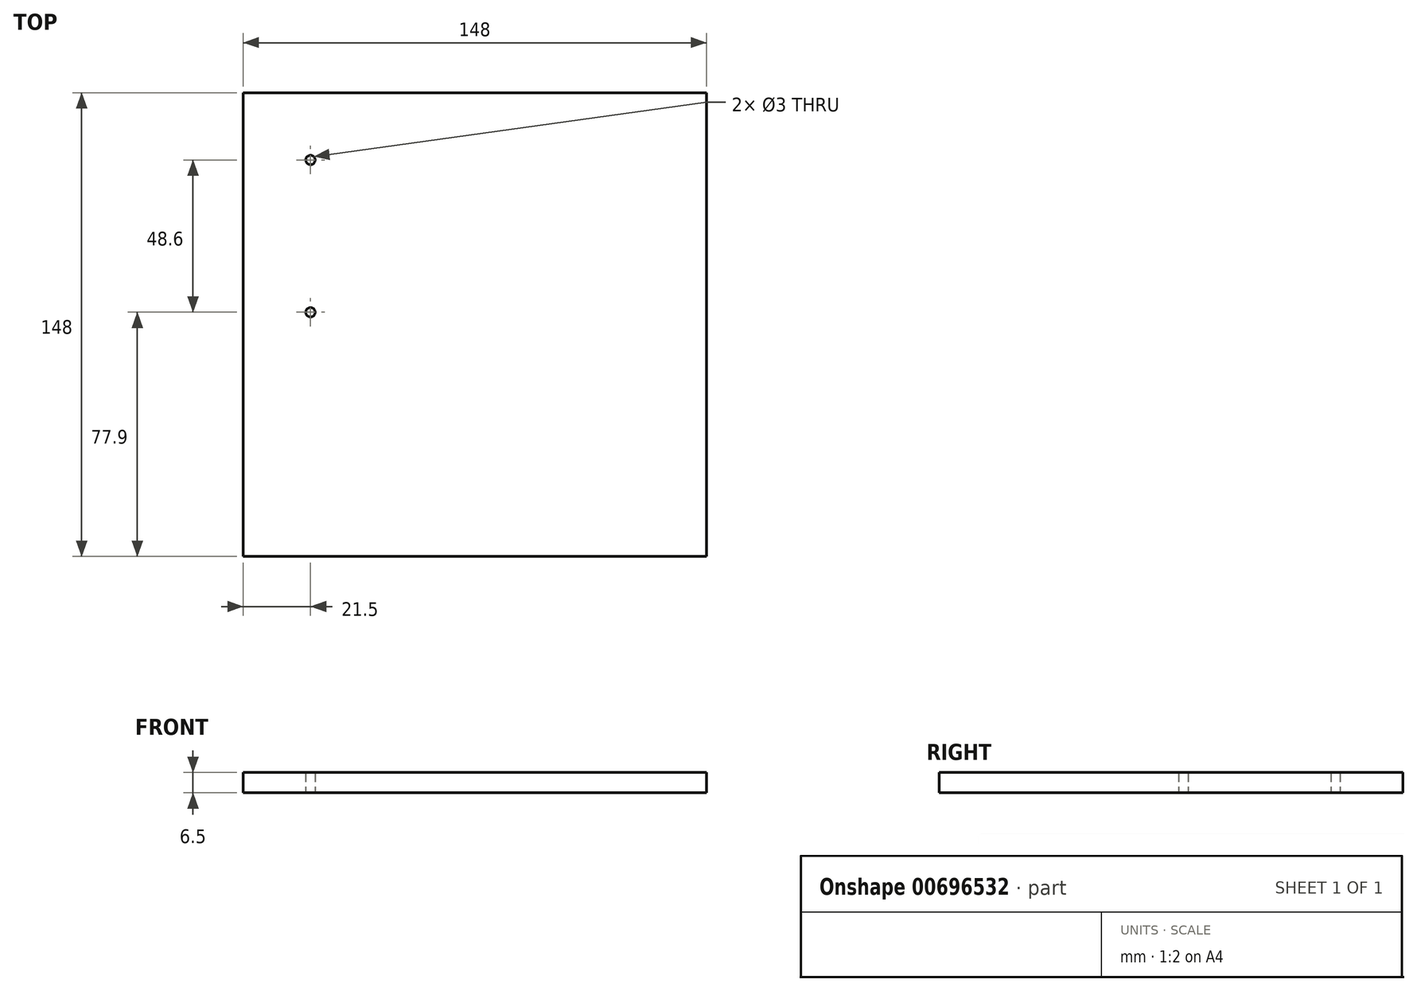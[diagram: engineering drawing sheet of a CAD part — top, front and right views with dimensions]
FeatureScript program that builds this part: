
annotation { "Feature Type Name" : "Feature", "Feature Type Description" : "" }
export const myFeature = defineFeature(function(context is Context, id is Id, definition is map)
    precondition{}
    {
        {
            var Q0;
            Q0=qCreatedBy(makeId("Top.planeOp"),FACE);
            var sketch = newSketch(context, id + "F0", { "sketchPlane" : qUnion([Q0])});
            skLineSegment(sketch, "E0.bottom", {"start": v(74, -74) * mm, "end": v(-74, -74) * mm});
            skLineSegment(sketch, "E0.top", {"start": v(74, 74) * mm, "end": v(-74, 74) * mm});
            skLineSegment(sketch, "E0.left", {"start": v(74, -74) * mm, "end": v(74, 74) * mm});
            skLineSegment(sketch, "E0.right", {"start": v(-74, -74) * mm, "end": v(-74, 74) * mm});
            skPoint(sketch, "E0.middle", {"position": v(0, 0) * mm});
            skCircle(sketch, "E1", {"center": v(-52.5, 52.5) * mm, "radius": 1.5 * mm});
            skCircle(sketch, "E2", {"center": v(-52.5, 3.9) * mm, "radius": 1.5 * mm});
            skSolve(sketch);
        }
        {
            var Q0;
            Q0=makeQuery(id+"F0.imprint","IMPRINT",FACE,{"disambiguationData":[TD([[makeQuery(id+"F0.imprint","IMPRINT",EDGE,{"derivedFrom":sQuery(id+"F0.wireOp",EDGE,"E0.bottom")}),-1.0]])]});
            extrude(context, id + "F1", {"entities" : qUnion([Q0]), "depth" : 6.5 * mm, "offsetDistance" : 25 * mm});
        }
    });
